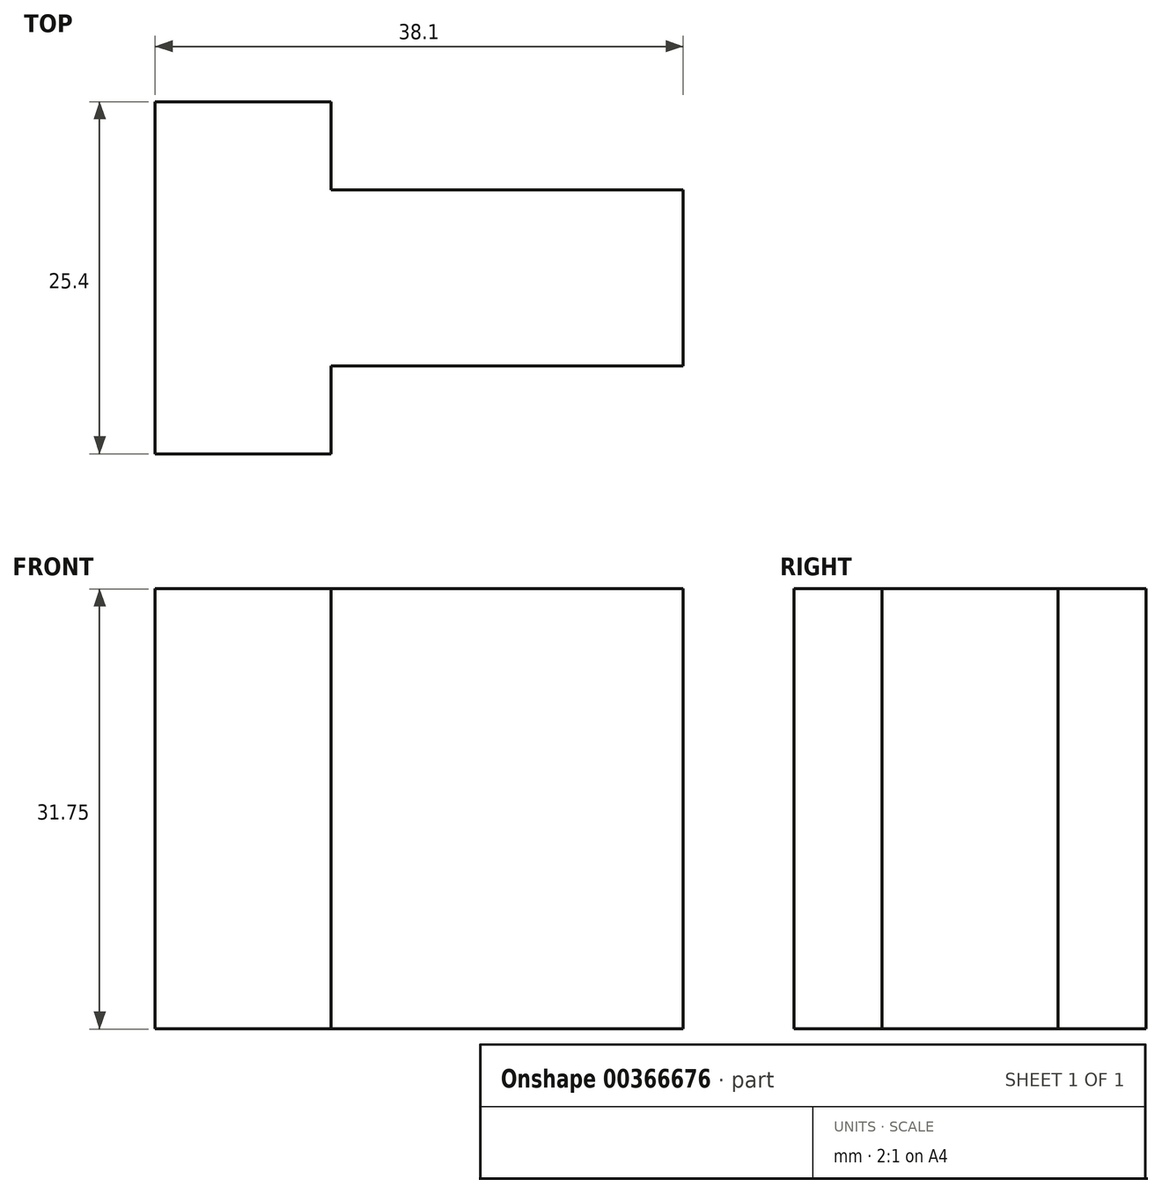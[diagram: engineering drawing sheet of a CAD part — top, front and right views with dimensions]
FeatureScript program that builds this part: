
annotation { "Feature Type Name" : "Feature", "Feature Type Description" : "" }
export const myFeature = defineFeature(function(context is Context, id is Id, definition is map)
    precondition{}
    {
        {
            var Q0;
            Q0=qCreatedBy(makeId("Front.planeOp"),FACE);
            var sketch = newSketch(context, id + "F0", { "sketchPlane" : qUnion([Q0])});
            skLineSegment(sketch, "E0", {"start": v(-56.44, 31.95) * mm, "end": v(-18.34, 31.95) * mm});
            skLineSegment(sketch, "E1", {"start": v(-18.34, 31.95) * mm, "end": v(-18.34, 0.2) * mm});
            skLineSegment(sketch, "E2", {"start": v(-18.34, 0.2) * mm, "end": v(-56.44, 0.2) * mm});
            skLineSegment(sketch, "E3", {"start": v(-56.44, 31.95) * mm, "end": v(-56.44, 0.2) * mm});
            skSolve(sketch);
        }
        {
            var Q0;
            Q0=makeQuery(id+"F0.imprint","IMPRINT",FACE,{"disambiguationData":[TD([[makeQuery(id+"F0.imprint","IMPRINT",EDGE,{"derivedFrom":sQuery(id+"F0.wireOp",EDGE,"E0")}),-1.0]])]});
            var Q1;
            Q1 = qSketchRegion(id + "F9YvTfVW7HVzwns_1", true);
            extrude(context, id + "F1", {"entities" : qUnion([Q0, Q1]), "depth" : 25.4 * mm});
        }
        {
            var Q0;
            Q0=makeQuery(id+"F1.opExtrude","CAP_FACE",FACE,{"disambiguationData":[OSD([sQuery(id+"F0.wireOp",EDGE,"E0"),sQuery(id+"F0.wireOp",EDGE,"E1"),sQuery(id+"F0.wireOp",EDGE,"E2"),sQuery(id+"F0.wireOp",EDGE,"E3")])],"isStart":false});
            var sketch = newSketch(context, id + "F2", { "sketchPlane" : qUnion([Q0])});
            skLineSegment(sketch, "E4", {"start": v(-43.74, 31.95) * mm, "end": v(-43.74, 0.2) * mm});
            skPoint(sketch, "E4.endSnap0", {"position": v(-37.39, 0.2) * mm});
            skSolve(sketch);
        }
        {
            var Q0;
            {var subQ0=sQuery(id+"F2.wireOp",EDGE,"E4");Q0=makeQuery(id+"F2.imprint","IMPRINT",FACE,{"disambiguationData":[TD([[makeQuery(id+"F2.imprint","IMPRINT",EDGE,{"derivedFrom":subQ0}),1.0]])]});}
            extrude(context, id + "F3", {"entities" : qUnion([Q0]), "operationType" : NewBodyOperationType.REMOVE, "oppositeDirection" : true, "depth" : 6.35 * mm});
        }
        {
            var Q0;
            Q0=makeQuery(id+"F1.opExtrude","CAP_FACE",FACE,{"disambiguationData":[OSD([sQuery(id+"F0.wireOp",EDGE,"E0"),sQuery(id+"F0.wireOp",EDGE,"E1"),sQuery(id+"F0.wireOp",EDGE,"E2"),sQuery(id+"F0.wireOp",EDGE,"E3")])],"isStart":true});
            var sketch = newSketch(context, id + "F4", { "sketchPlane" : qUnion([Q0])});
            skLineSegment(sketch, "E5", {"start": v(43.74, 31.95) * mm, "end": v(43.74, 0) * mm});
            skSolve(sketch);
        }
        {
            var Q0;
            {var subQ5=makeQuery(id+"F1.opExtrude","CAP_EDGE",EDGE,{"disambiguationData":[OSD([sQuery(id+"F0.wireOp",EDGE,"E1")])],"isStart":true});Q0=makeQuery(id+"F4.imprint","IMPRINT",FACE,{"disambiguationData":[TD([[makeQuery(id+"F4.imprint","IMPRINT",EDGE,{"derivedFrom":subQ5}),1.0]])]});}
            extrude(context, id + "F5", {"entities" : qUnion([Q0]), "operationType" : NewBodyOperationType.REMOVE, "oppositeDirection" : true, "depth" : 6.35 * mm});
        }
    });
